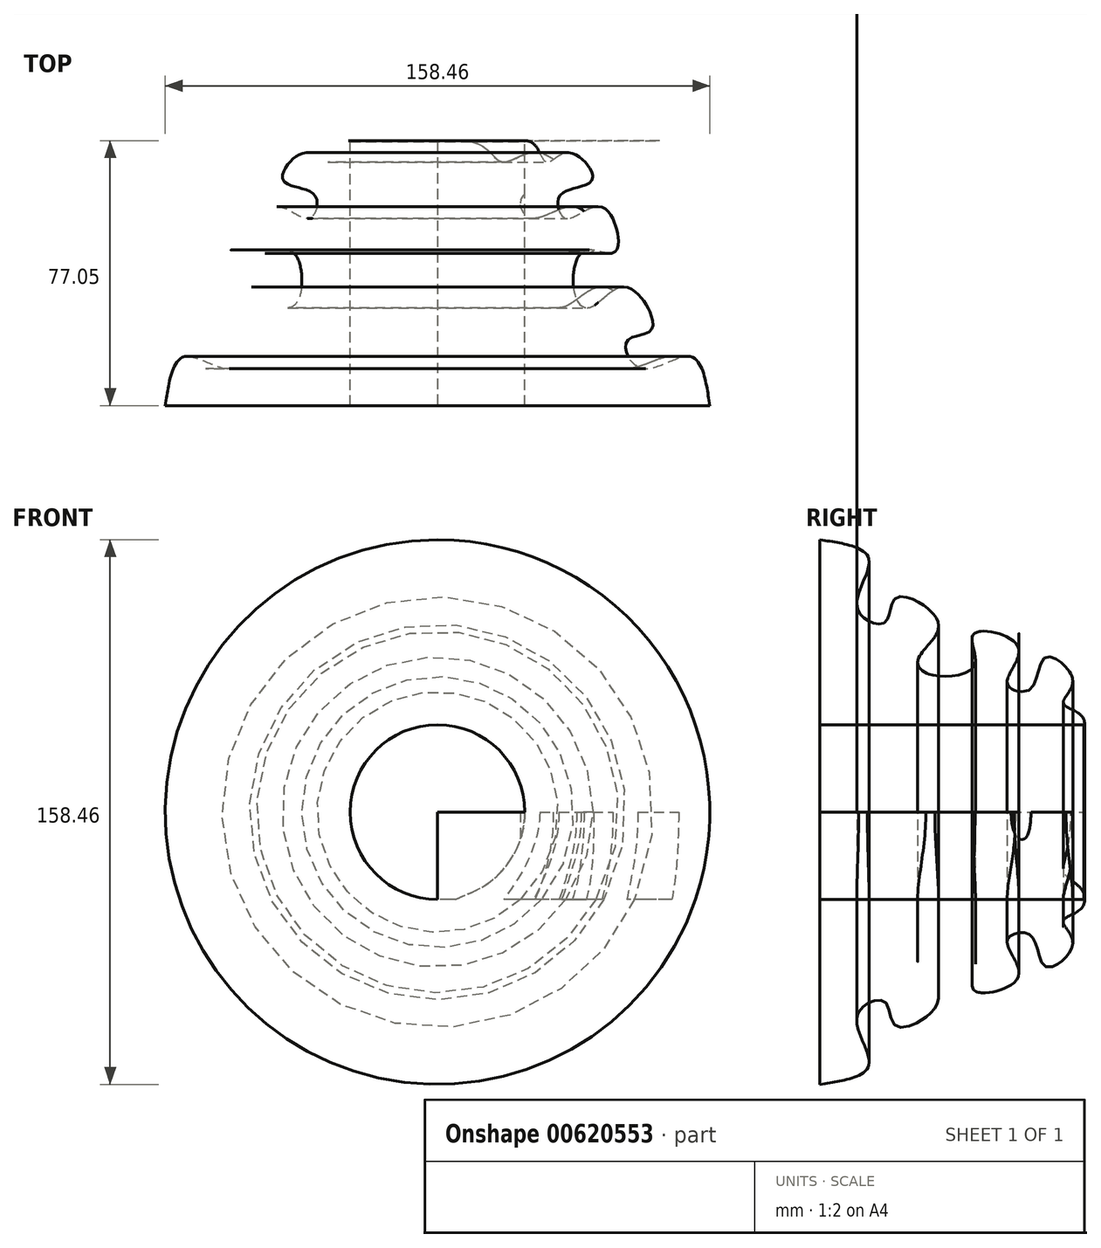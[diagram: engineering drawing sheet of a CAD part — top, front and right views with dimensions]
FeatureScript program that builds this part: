
annotation { "Feature Type Name" : "Feature", "Feature Type Description" : "" }
export const myFeature = defineFeature(function(context is Context, id is Id, definition is map)
    precondition{}
    {
        {
            var Q0;
            Q0=qCreatedBy(makeId("Top.planeOp"),FACE);
            var sketch = newSketch(context, id + "F0", { "sketchPlane" : qUnion([Q0])});
            skLineSegment(sketch, "E0", {"start": v(0, 0) * mm, "end": v(75.05, 0) * mm});
            skLineSegment(sketch, "E1", {"start": v(0, 76.85) * mm, "end": v(0, 0) * mm});
            skFitSpline(sketch, "E2", {"points": [v(75.05, 0) * mm, v(69.03, 14.29) * mm, v(53.4, 10.98) * mm, v(48.88, 18.8) * mm, v(57, 22.4) * mm, v(48.88, 34.44) * mm, v(36.85, 28.73) * mm, v(30.83, 32.33) * mm, v(34.14, 44.97) * mm, v(45.27, 44.97) * mm, v(41.06, 57.6) * mm, v(27.22, 54.6) * mm, v(24.82, 60.9) * mm, v(37.15, 65.72) * mm, v(29.33, 73.54) * mm, v(19.1, 70.84) * mm, v(13.39, 75.35) * mm, v(0, 76.85) * mm], "startDerivative": vector(-46.44, 296.66) * mm, "endDerivative": vector(-240.02, -13.3) * mm});
            skSolve(sketch);
        }
        {
            var Q0;
            Q0 = qSketchRegion(id + "F0", true);
            extrude(context, id + "F1", {"entities" : qUnion([Q0]), "depth" : 25.4 * mm, "offsetDistance" : 25.4 * mm});
        }
        {
            var Q0;
            Q0=makeQuery(id+"F1.opExtrude","CAP_FACE",FACE,{"disambiguationData":[OSD([sQuery(id+"F0.wireOp",EDGE,"E0"),sQuery(id+"F0.wireOp",EDGE,"E1"),sQuery(id+"F0.wireOp",EDGE,"E2")])],"isStart":true});
            var Q1;
            Q1=makeQuery(id+"F1.opExtrude","CAP_EDGE",EDGE,{"disambiguationData":[OSD([sQuery(id+"F0.wireOp",EDGE,"E1")])],"isStart":false});
            revolve(context, id + "F2", {"operationType" : NewBodyOperationType.ADD, "entities" : qUnion([Q0]), "axis" : qUnion([Q1]), "revolveType" : RevolveType.FULL});
        }
    });
